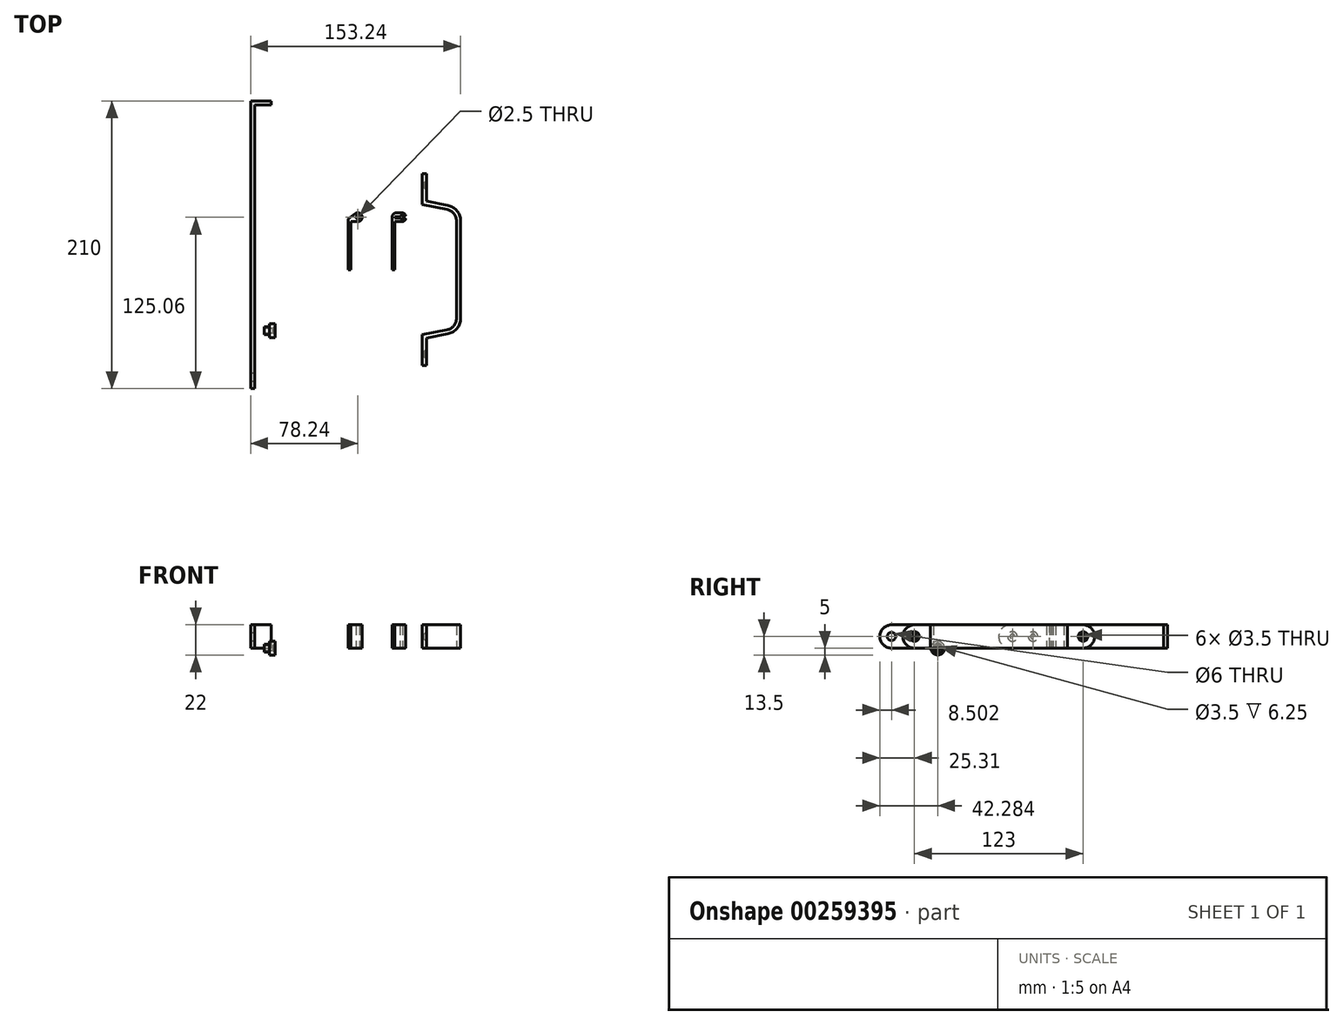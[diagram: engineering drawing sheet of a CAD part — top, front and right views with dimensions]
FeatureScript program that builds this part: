
annotation { "Feature Type Name" : "Feature", "Feature Type Description" : "" }
export const myFeature = defineFeature(function(context is Context, id is Id, definition is map)
    precondition{}
    {
        {
            var Q0;
            Q0=qCreatedBy(makeId("Top.planeOp"),FACE);
            var sketch = newSketch(context, id + "F0", { "sketchPlane" : qUnion([Q0])});
            skCircle(sketch, "E0", {"center": v(6, 20.75) * mm, "radius": 1.25 * mm});
            skArc(sketch, "E1", {"start": v(6, 17.5) * mm, "mid": v(9.08, 21.79) * mm, "end": v(4.03, 23.33) * mm});
            skLineSegment(sketch, "E2", {"start": v(4.03, 23.33) * mm, "end": v(-1, 19.5) * mm});
            skLineSegment(sketch, "E3", {"start": v(-1, 19.5) * mm, "end": v(-1, -17.5) * mm});
            skLineSegment(sketch, "E4", {"start": v(-1, -17.5) * mm, "end": v(1, -17.5) * mm});
            skLineSegment(sketch, "E5", {"start": v(1, -17.5) * mm, "end": v(1, 17.5) * mm});
            skLineSegment(sketch, "E6", {"start": v(1, 17.5) * mm, "end": v(6, 17.5) * mm});
            skArc(sketch, "E7", {"start": v(38, 17.5) * mm, "mid": v(39.91, 18.12) * mm, "end": v(41.1, 19.75) * mm});
            skLineSegment(sketch, "E8", {"start": v(38, 24) * mm, "end": v(34.25, 24) * mm});
            skLineSegment(sketch, "E9", {"start": v(31, 20.75) * mm, "end": v(31, -17.5) * mm});
            skLineSegment(sketch, "E10", {"start": v(31, -17.5) * mm, "end": v(33, -17.5) * mm});
            skLineSegment(sketch, "E11", {"start": v(33, -17.5) * mm, "end": v(33, 17.5) * mm});
            skLineSegment(sketch, "E12", {"start": v(33, 17.5) * mm, "end": v(38, 17.5) * mm});
            skLineSegment(sketch, "E13", {"start": v(41.25, 20.75) * mm, "end": v(31, 20.75) * mm, "construction": true});
            skLineSegment(sketch, "E14", {"start": v(33, 21.25) * mm, "end": v(36.85, 21.25) * mm});
            skLineSegment(sketch, "E15", {"start": v(38.75, 21.75) * mm, "end": v(41.1, 21.75) * mm});
            skLineSegment(sketch, "E16.MirrorCS", {"start": v(38.75, 19.75) * mm, "end": v(41.1, 19.75) * mm});
            skLineSegment(sketch, "E17.MirrorCS", {"start": v(33, 20.25) * mm, "end": v(36.85, 20.25) * mm});
            skArc(sketch, "E18", {"start": v(36.85, 21.25) * mm, "mid": v(36.75, 20.75) * mm, "end": v(36.85, 20.25) * mm, "construction": true});
            skArc(sketch, "E19", {"start": v(38.75, 21.75) * mm, "mid": v(37.68, 21.96) * mm, "end": v(36.85, 21.25) * mm});
            skArc(sketch, "E20", {"start": v(38.75, 19.75) * mm, "mid": v(39.25, 20.75) * mm, "end": v(38.75, 21.75) * mm, "construction": true});
            skArc(sketch, "E21", {"start": v(36.85, 20.25) * mm, "mid": v(37.68, 19.54) * mm, "end": v(38.75, 19.75) * mm});
            skArc(sketch, "E22", {"start": v(41.1, 21.75) * mm, "mid": v(39.91, 23.38) * mm, "end": v(38, 24) * mm});
            skArc(sketch, "E23", {"start": v(41.1, 19.75) * mm, "mid": v(41.25, 20.75) * mm, "end": v(41.1, 21.75) * mm, "construction": true});
            skLineSegment(sketch, "E24", {"start": v(33, 21.25) * mm, "end": v(33, 20.25) * mm});
            skPoint(sketch, "E25.visualSharp", {"position": v(31, 24) * mm});
            skArc(sketch, "E25.filletArc", {"start": v(34.25, 24) * mm, "mid": v(31.95, 23.05) * mm, "end": v(31, 20.75) * mm});
            skLineSegment(sketch, "E26", {"start": v(56, 52.5) * mm, "end": v(56, 32.5) * mm});
            skLineSegment(sketch, "E27", {"start": v(56, 32.5) * mm, "end": v(81, 27.5) * mm});
            skLineSegment(sketch, "E28", {"start": v(81, 27.5) * mm, "end": v(81, -17.5) * mm});
            skLineSegment(sketch, "E29.0", {"start": v(78, 25.04) * mm, "end": v(78, -17.5) * mm});
            skLineSegment(sketch, "E29.1", {"start": v(53, 30.04) * mm, "end": v(78, 25.04) * mm});
            skLineSegment(sketch, "E29.2", {"start": v(53, 52.5) * mm, "end": v(53, 30.04) * mm});
            skLineSegment(sketch, "E30", {"start": v(53, 52.5) * mm, "end": v(56, 52.5) * mm});
            skLineSegment(sketch, "E31", {"start": v(78, -17.5) * mm, "end": v(81, -17.5) * mm, "construction": true});
            skLineSegment(sketch, "E32.MirrorCS", {"start": v(81, -62.5) * mm, "end": v(81, -17.5) * mm});
            skLineSegment(sketch, "E33.MirrorCS", {"start": v(78, -60.04) * mm, "end": v(78, -17.5) * mm});
            skLineSegment(sketch, "E34.MirrorCS", {"start": v(56, -67.5) * mm, "end": v(81, -62.5) * mm});
            skLineSegment(sketch, "E35.MirrorCS", {"start": v(53, -65.04) * mm, "end": v(78, -60.04) * mm});
            skLineSegment(sketch, "E36.MirrorCS", {"start": v(53, -87.5) * mm, "end": v(53, -65.04) * mm});
            skLineSegment(sketch, "E37.MirrorCS", {"start": v(56, -87.5) * mm, "end": v(56, -67.5) * mm});
            skLineSegment(sketch, "E38.MirrorCS", {"start": v(53, -87.5) * mm, "end": v(56, -87.5) * mm});
            skLineSegment(sketch, "E39", {"start": v(-72.24, -104.3) * mm, "end": v(-72.24, 105.7) * mm});
            skLineSegment(sketch, "E40", {"start": v(-72.24, 105.7) * mm, "end": v(-57.24, 105.7) * mm});
            skLineSegment(sketch, "E41.0", {"start": v(-69.24, 102.7) * mm, "end": v(-57.24, 102.7) * mm});
            skLineSegment(sketch, "E41.1", {"start": v(-69.24, -104.3) * mm, "end": v(-69.24, 102.7) * mm});
            skLineSegment(sketch, "E42", {"start": v(-57.24, 105.7) * mm, "end": v(-57.24, 102.7) * mm});
            skLineSegment(sketch, "E43", {"start": v(-72.24, -104.3) * mm, "end": v(-69.24, -104.3) * mm});
            skSolve(sketch);
        }
        {
            var Q0;
            Q0 = qSketchRegion(id + "F0", true);
            extrude(context, id + "F1", {"entities" : qUnion([Q0]), "depth" : 17 * mm});
        }
        {
            var Q0;
            Q0=makeQuery(id+"F1.opExtrude","SWEPT_FACE",FACE,{"disambiguationData":[OSD([sQuery(id+"F0.wireOp",EDGE,"E3")])]});
            var sketch = newSketch(context, id + "F2", { "sketchPlane" : qUnion([Q0])});
            skLineSegment(sketch, "E44.0", {"start": v(17.5, 17) * mm, "end": v(-17.5, 17) * mm, "construction": true});
            skLineSegment(sketch, "E44.1", {"start": v(17.5, 17) * mm, "end": v(17.5, 0) * mm, "construction": true});
            skLineSegment(sketch, "E44.2", {"start": v(17.5, 0) * mm, "end": v(-17.5, 0) * mm, "construction": true});
            skPoint(sketch, "E45", {"position": v(7.5, 8.5) * mm});
            skPoint(sketch, "E45.positionSnap0", {"position": v(17.5, 8.5) * mm});
            skPoint(sketch, "E46", {"position": v(-7.5, 8.5) * mm});
            skSolve(sketch);
        }
        {
            var Q0;
            Q0=makeQuery(id+"F1.opExtrude","SWEPT_FACE",FACE,{"disambiguationData":[OSD([sQuery(id+"F0.wireOp",EDGE,"E9")])]});
            var sketch = newSketch(context, id + "F3", { "sketchPlane" : qUnion([Q0])});
            skLineSegment(sketch, "E47.0", {"start": v(17.5, 17) * mm, "end": v(-17.5, 17) * mm, "construction": true});
            skLineSegment(sketch, "E47.1", {"start": v(17.5, 17) * mm, "end": v(17.5, 0) * mm, "construction": true});
            skLineSegment(sketch, "E47.2", {"start": v(17.5, 0) * mm, "end": v(-17.5, 0) * mm, "construction": true});
            skPoint(sketch, "E48.0", {"position": v(7.5, 8.5) * mm});
            skPoint(sketch, "E48.1", {"position": v(-7.5, 8.5) * mm});
            skSolve(sketch);
        }
        {
            var Q0;
            Q0=makeQuery(id+"F1.opExtrude","CAP_EDGE",EDGE,{"disambiguationData":[OSD([sQuery(id+"F0.wireOp",EDGE,"E4")])],"isStart":false});
            var Q1;
            Q1=makeQuery(id+"F1.opExtrude","CAP_EDGE",EDGE,{"disambiguationData":[OSD([sQuery(id+"F0.wireOp",EDGE,"E4")])],"isStart":true});
            var Q2;
            Q2=makeQuery(id+"F1.opExtrude","CAP_EDGE",EDGE,{"disambiguationData":[OSD([sQuery(id+"F0.wireOp",EDGE,"E10")])],"isStart":false});
            var Q3;
            Q3=makeQuery(id+"F1.opExtrude","CAP_EDGE",EDGE,{"disambiguationData":[OSD([sQuery(id+"F0.wireOp",EDGE,"E10")])],"isStart":true});
            var Q4;
            Q4=makeQuery(id+"F1.opExtrude","CAP_EDGE",EDGE,{"disambiguationData":[OSD([sQuery(id+"F0.wireOp",EDGE,"E30")])],"isStart":false});
            var Q5;
            Q5=makeQuery(id+"F1.opExtrude","CAP_EDGE",EDGE,{"disambiguationData":[OSD([sQuery(id+"F0.wireOp",EDGE,"E30")])],"isStart":true});
            var Q6;
            Q6=makeQuery(id+"F1.opExtrude","CAP_EDGE",EDGE,{"disambiguationData":[OSD([sQuery(id+"F0.wireOp",EDGE,"E38.MirrorCS")])],"isStart":false});
            var Q7;
            Q7=makeQuery(id+"F1.opExtrude","CAP_EDGE",EDGE,{"disambiguationData":[OSD([sQuery(id+"F0.wireOp",EDGE,"E38.MirrorCS")])],"isStart":true});
            var Q8;
            Q8=makeQuery(id+"F1.opExtrude","SWEPT_EDGE",EDGE,{"disambiguationData":[OSD([sQuery(id+"F0.wireOp",EDGE,"E33.MirrorCS"),sQuery(id+"F0.wireOp",EDGE,"E35.MirrorCS")])]});
            var Q9;
            Q9=makeQuery(id+"F1.opExtrude","SWEPT_EDGE",EDGE,{"disambiguationData":[OSD([sQuery(id+"F0.wireOp",EDGE,"E29.0"),sQuery(id+"F0.wireOp",EDGE,"E29.1")])]});
            var Q10;
            Q10=makeQuery(id+"F1.opExtrude","CAP_EDGE",EDGE,{"disambiguationData":[OSD([sQuery(id+"F0.wireOp",EDGE,"E43")])],"isStart":false});
            var Q11;
            Q11=makeQuery(id+"F1.opExtrude","CAP_EDGE",EDGE,{"disambiguationData":[OSD([sQuery(id+"F0.wireOp",EDGE,"E43")])],"isStart":true});
            fillet(context, id + "F4", {"entities" : qUnion([Q0, Q1, Q2, Q3, Q4, Q5, Q6, Q7, Q8, Q9, Q10, Q11]), "radius" : 8.5 * mm, "tangentPropagation" : true, "allowEdgeOverflow" : false});
        }
        {
            var Q0;
            Q0=makeQuery(id+"F1.opExtrude","SWEPT_EDGE",EDGE,{"disambiguationData":[OSD([sQuery(id+"F0.wireOp",EDGE,"E7"),sQuery(id+"F0.wireOp",EDGE,"E16.MirrorCS")])]});
            var Q1;
            Q1=makeQuery(id+"F1.opExtrude","SWEPT_EDGE",EDGE,{"disambiguationData":[OSD([sQuery(id+"F0.wireOp",EDGE,"E15"),sQuery(id+"F0.wireOp",EDGE,"E22")])]});
            fillet(context, id + "F5", {"entities" : qUnion([Q0, Q1]), "radius" : 0.5 * mm, "tangentPropagation" : true, "allowEdgeOverflow" : false});
        }
        {
            var Q0;
            Q0=makeQuery(id+"F1.opExtrude","SWEPT_FACE",FACE,{"disambiguationData":[OSD([sQuery(id+"F0.wireOp",EDGE,"E37.MirrorCS")])]});
            var sketch = newSketch(context, id + "F6", { "sketchPlane" : qUnion([Q0])});
            skArc(sketch, "E49.0", {"start": v(44, 0) * mm, "mid": v(52.5, 8.5) * mm, "end": v(44, 17) * mm, "construction": true});
            skArc(sketch, "E49.1", {"start": v(-79, 17) * mm, "mid": v(-87.5, 8.5) * mm, "end": v(-79, 0) * mm, "construction": true});
            skSolve(sketch);
        }
        {
            var Q0;
            Q0=sQuery(id+"F2.wireOp",VERTEX,"E45");
            var Q1;
            Q1=sQuery(id+"F2.wireOp",VERTEX,"E46");
            var Q2;
            Q2=sQuery(id+"F3.wireOp",VERTEX,"E48.0");
            var Q3;
            Q3=sQuery(id+"F3.wireOp",VERTEX,"E48.1");
            var Q4;
            Q4=sQuery(id+"F6.wireOp",VERTEX,"E49.0.center");
            var Q5;
            Q5=sQuery(id+"F6.wireOp",VERTEX,"E49.1.center");
            var Q6;
            Q6=makeQuery(id+"F1.opExtrude","SWEPT_BODY",BODY,{"disambiguationData":[OSD([sQuery(id+"F0.wireOp",EDGE,"E0"),sQuery(id+"F0.wireOp",EDGE,"E1"),sQuery(id+"F0.wireOp",EDGE,"E2"),sQuery(id+"F0.wireOp",EDGE,"E3"),sQuery(id+"F0.wireOp",EDGE,"E4"),sQuery(id+"F0.wireOp",EDGE,"E5"),sQuery(id+"F0.wireOp",EDGE,"E6")])]});
            var Q7;
            Q7=makeQuery(id+"F1.opExtrude","SWEPT_BODY",BODY,{"disambiguationData":[OSD([sQuery(id+"F0.wireOp",EDGE,"E7"),sQuery(id+"F0.wireOp",EDGE,"E8"),sQuery(id+"F0.wireOp",EDGE,"E9"),sQuery(id+"F0.wireOp",EDGE,"E10"),sQuery(id+"F0.wireOp",EDGE,"E11"),sQuery(id+"F0.wireOp",EDGE,"E12"),sQuery(id+"F0.wireOp",EDGE,"E14"),sQuery(id+"F0.wireOp",EDGE,"E15"),sQuery(id+"F0.wireOp",EDGE,"E16.MirrorCS"),sQuery(id+"F0.wireOp",EDGE,"E17.MirrorCS"),sQuery(id+"F0.wireOp",EDGE,"E19"),sQuery(id+"F0.wireOp",EDGE,"E21"),sQuery(id+"F0.wireOp",EDGE,"E22"),sQuery(id+"F0.wireOp",EDGE,"E24"),sQuery(id+"F0.wireOp",EDGE,"E25.filletArc")])]});
            var Q8;
            Q8=makeQuery(id+"F1.opExtrude","SWEPT_BODY",BODY,{"disambiguationData":[OSD([sQuery(id+"F0.wireOp",EDGE,"E26"),sQuery(id+"F0.wireOp",EDGE,"E27"),sQuery(id+"F0.wireOp",EDGE,"E28"),sQuery(id+"F0.wireOp",EDGE,"E29.0"),sQuery(id+"F0.wireOp",EDGE,"E29.1"),sQuery(id+"F0.wireOp",EDGE,"E29.2"),sQuery(id+"F0.wireOp",EDGE,"E30"),sQuery(id+"F0.wireOp",EDGE,"E32.MirrorCS"),sQuery(id+"F0.wireOp",EDGE,"E33.MirrorCS"),sQuery(id+"F0.wireOp",EDGE,"E34.MirrorCS"),sQuery(id+"F0.wireOp",EDGE,"E35.MirrorCS"),sQuery(id+"F0.wireOp",EDGE,"E36.MirrorCS"),sQuery(id+"F0.wireOp",EDGE,"E37.MirrorCS"),sQuery(id+"F0.wireOp",EDGE,"E38.MirrorCS")])]});
            hole(context, id + "F7", {"style" : HoleStyle.C_SINK, "endStyle" : HoleEndStyle.BLIND, "holeDiameter" : 3.5 * mm, "cSinkDiameter" : 7 * mm, "cSinkAngle" : 90 * degree, "holeDepth" : 20 * mm, "tappedDepth" : 12 * mm, "tapClearance" : 3, "startFromSketch" : true, "locations" : qUnion([Q0, Q1, Q2, Q3, Q4, Q5]), "scope" : qUnion([Q6, Q7, Q8])});
        }
        {
            var Q0;
            Q0=makeQuery(id+"F1.opExtrude","SWEPT_EDGE",EDGE,{"disambiguationData":[OSD([sQuery(id+"F0.wireOp",EDGE,"E32.MirrorCS"),sQuery(id+"F0.wireOp",EDGE,"E34.MirrorCS")])]});
            var Q1;
            Q1=makeQuery(id+"F1.opExtrude","SWEPT_EDGE",EDGE,{"disambiguationData":[OSD([sQuery(id+"F0.wireOp",EDGE,"E27"),sQuery(id+"F0.wireOp",EDGE,"E28")])]});
            fillet(context, id + "F8", {"entities" : qUnion([Q0, Q1]), "radius" : 11.5 * mm, "tangentPropagation" : true, "allowEdgeOverflow" : false});
        }
        {
            var Q0;
            Q0=makeQuery(id+"F1.opExtrude","SWEPT_FACE",FACE,{"disambiguationData":[OSD([sQuery(id+"F0.wireOp",EDGE,"E41.1")])]});
            var sketch = newSketch(context, id + "F9", { "sketchPlane" : qUnion([Q0])});
            skArc(sketch, "E50.0", {"start": v(-95.8, 17) * mm, "mid": v(-104.3, 8.5) * mm, "end": v(-95.8, 0) * mm, "construction": true});
            skCircle(sketch, "E51", {"center": v(-95.8, 8.5) * mm, "radius": 3 * mm});
            skSolve(sketch);
        }
        {
            var Q0;
            Q0 = qSketchRegion(id + "F9", true);
            extrude(context, id + "F10", {"entities" : qUnion([Q0]), "operationType" : NewBodyOperationType.REMOVE, "oppositeDirection" : true, "depth" : 25 * mm});
        }
        {
            var Q0;
            Q0=qCreatedBy(makeId("Top.planeOp"),FACE);
            var sketch = newSketch(context, id + "F11", { "sketchPlane" : qUnion([Q0])});
            skLineSegment(sketch, "E52", {"start": v(-66.8, -62.03) * mm, "end": v(-46.17, -62.03) * mm, "construction": true});
            skLineSegment(sketch, "E53", {"start": v(-62.3, -62.03) * mm, "end": v(-62.3, -59.28) * mm});
            skLineSegment(sketch, "E54", {"start": v(-62.3, -59.28) * mm, "end": v(-58.3, -59.28) * mm});
            skLineSegment(sketch, "E55", {"start": v(-58.3, -59.28) * mm, "end": v(-58.3, -57.03) * mm});
            skLineSegment(sketch, "E56", {"start": v(-58.3, -57.03) * mm, "end": v(-54.3, -57.03) * mm});
            skLineSegment(sketch, "E57", {"start": v(-54.3, -57.03) * mm, "end": v(-54.3, -62.03) * mm});
            skLineSegment(sketch, "E58", {"start": v(-62.3, -62.03) * mm, "end": v(-54.3, -62.03) * mm});
            skSolve(sketch);
        }
        {
            var Q0;
            Q0=makeQuery(id+"F11.imprint","IMPRINT",FACE,{"disambiguationData":[TD([[makeQuery(id+"F11.imprint","IMPRINT",EDGE,{"derivedFrom":sQuery(id+"F11.wireOp",EDGE,"E53")}),-1.0]])]});
            var Q1;
            Q1=sQuery(id+"F11.wireOp",EDGE,"E52");
            revolve(context, id + "F12", {"entities" : qUnion([Q0]), "axis" : qUnion([Q1]), "revolveType" : RevolveType.FULL});
        }
        {
            var Q0;
            Q0=makeQuery(id+"F12.opRevolve","SWEPT_FACE",FACE,{"disambiguationData":[OSD([sQuery(id+"F11.wireOp",EDGE,"E57")])]});
            var sketch = newSketch(context, id + "F13", { "sketchPlane" : qUnion([Q0])});
            skPoint(sketch, "E59.0", {"position": v(-62.03, 0) * mm});
            skSolve(sketch);
        }
        {
            var Q0;
            Q0=sQuery(id+"F13.wireOp",VERTEX,"E59.0");
            var Q1;
            Q1=makeQuery(id+"F12.opRevolve","SWEPT_BODY",BODY,{"disambiguationData":[OSD([sQuery(id+"F11.wireOp",EDGE,"E53"),sQuery(id+"F11.wireOp",EDGE,"E54"),sQuery(id+"F11.wireOp",EDGE,"E55"),sQuery(id+"F11.wireOp",EDGE,"E56"),sQuery(id+"F11.wireOp",EDGE,"E57"),sQuery(id+"F11.wireOp",EDGE,"E58")])]});
            hole(context, id + "F14", {"style" : HoleStyle.C_SINK, "endStyle" : HoleEndStyle.BLIND, "holeDiameter" : 3.5 * mm, "cSinkDiameter" : 7 * mm, "cSinkAngle" : 90 * degree, "holeDepth" : 20 * mm, "tappedDepth" : 12 * mm, "tapClearance" : 3, "startFromSketch" : true, "locations" : qUnion([Q0]), "scope" : qUnion([Q1])});
        }
    });
